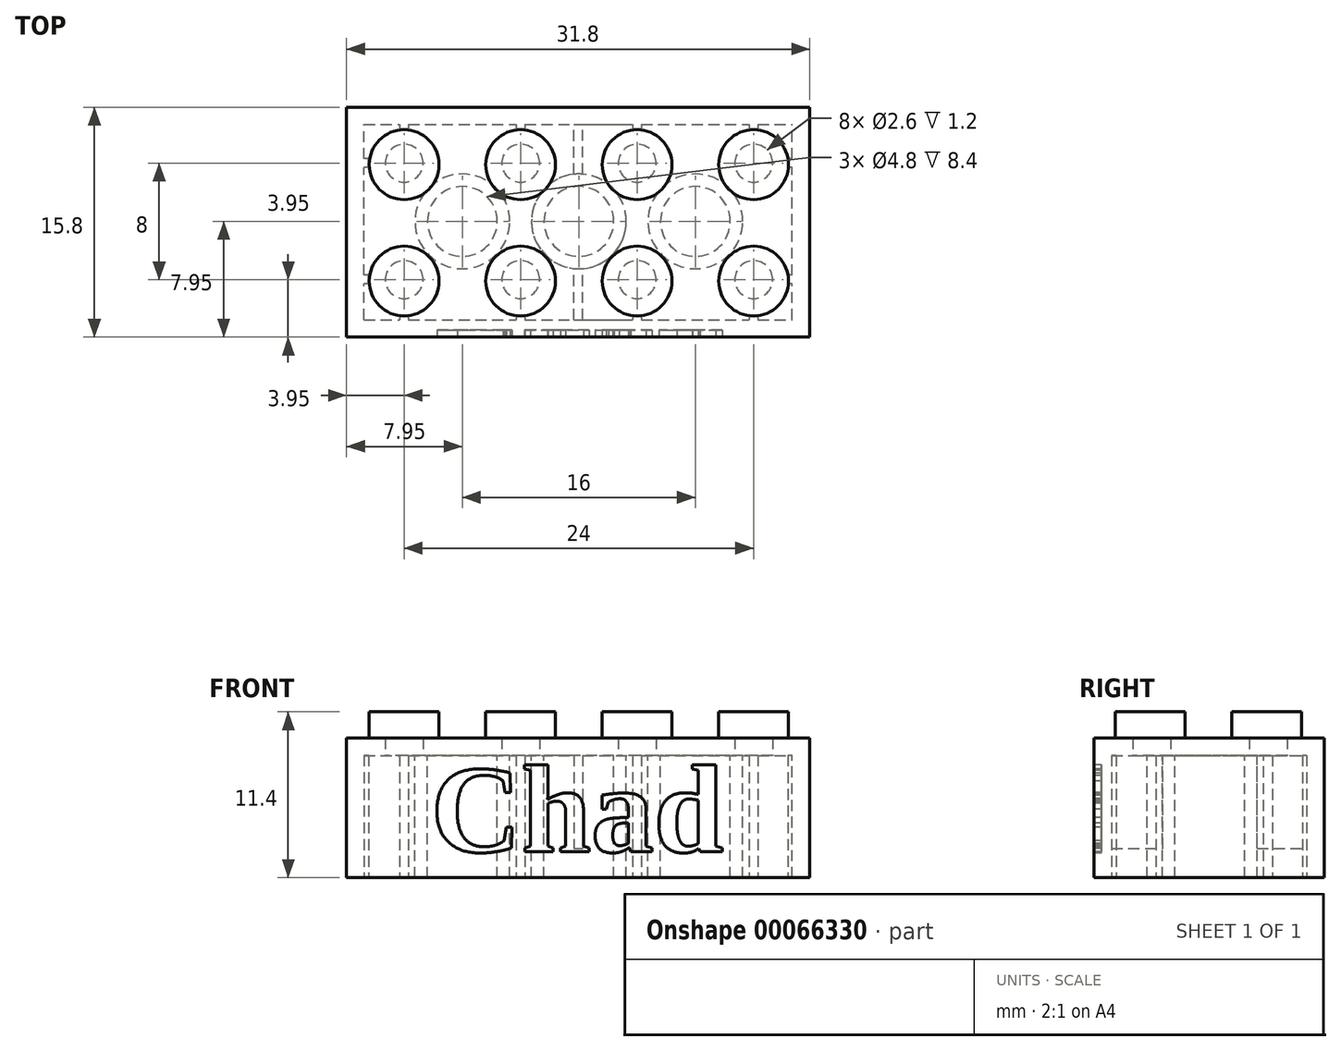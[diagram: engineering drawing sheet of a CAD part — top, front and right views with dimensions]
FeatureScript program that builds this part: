
annotation { "Feature Type Name" : "Feature", "Feature Type Description" : "" }
export const myFeature = defineFeature(function(context is Context, id is Id, definition is map)
    precondition{}
    {
        {
            var Q0;
            Q0=qCreatedBy(makeId("Top.planeOp"),FACE);
            var sketch = newSketch(context, id + "F0", { "sketchPlane" : qUnion([Q0])});
            skLineSegment(sketch, "E0.rect.bottom", {"start": v(15.9, 7.9) * mm, "end": v(-15.9, 7.9) * mm});
            skLineSegment(sketch, "E0.rect.top", {"start": v(15.9, -7.9) * mm, "end": v(-15.9, -7.9) * mm});
            skLineSegment(sketch, "E0.rect.left", {"start": v(15.9, 7.9) * mm, "end": v(15.9, -7.9) * mm});
            skLineSegment(sketch, "E0.rect.right", {"start": v(-15.9, 7.9) * mm, "end": v(-15.9, -7.9) * mm});
            skPoint(sketch, "E0.rect.middle", {"position": v(0, 0) * mm});
            skSolve(sketch);
        }
        {
            var Q0;
            Q0 = qSketchRegion(id + "F0", true);
            extrude(context, id + "F1", {"entities" : qUnion([Q0]), "depth" : 9.6 * mm});
        }
        {
            var Q0;
            Q0=makeQuery(id+"F0.imprint","IMPRINT",FACE,{"disambiguationData":[TD([[makeQuery(id+"F0.imprint","IMPRINT",EDGE,{"derivedFrom":sQuery(id+"F0.wireOp",EDGE,"E0.rect.bottom")}),1.0]])]});
            var sketch = newSketch(context, id + "F2", { "sketchPlane" : qUnion([Q0])});
            skLineSegment(sketch, "E1.rect.bottom", {"start": v(-14.7, -6.7) * mm, "end": v(14.7, -6.7) * mm});
            skLineSegment(sketch, "E1.rect.top", {"start": v(-14.7, 6.7) * mm, "end": v(14.7, 6.7) * mm});
            skLineSegment(sketch, "E1.rect.left", {"start": v(-14.7, -6.7) * mm, "end": v(-14.7, 6.7) * mm});
            skLineSegment(sketch, "E1.rect.right", {"start": v(14.7, -6.7) * mm, "end": v(14.7, 6.7) * mm});
            skPoint(sketch, "E1.rect.middle", {"position": v(0, 0) * mm});
            skSolve(sketch);
        }
        {
            var Q0;
            Q0 = qSketchRegion(id + "F2", true);
            extrude(context, id + "F3", {"entities" : qUnion([Q0]), "operationType" : NewBodyOperationType.REMOVE, "depth" : 8.4 * mm});
        }
        {
            var Q0;
            Q0=makeQuery(id+"F1.opExtrude","CAP_FACE",FACE,{"disambiguationData":[OSD([sQuery(id+"F0.wireOp",EDGE,"E0.rect.bottom"),sQuery(id+"F0.wireOp",EDGE,"E0.rect.top"),sQuery(id+"F0.wireOp",EDGE,"E0.rect.left"),sQuery(id+"F0.wireOp",EDGE,"E0.rect.right")])],"isStart":false});
            var sketch = newSketch(context, id + "F4", { "sketchPlane" : qUnion([Q0])});
            skLineSegment(sketch, "E2", {"start": v(-22.58, 0) * mm, "end": v(20.72, 0) * mm, "construction": true});
            skPoint(sketch, "E2.endSnap0", {"position": v(15.9, 0) * mm});
            skCircle(sketch, "E3", {"center": v(-11.95, 3.95) * mm, "radius": 2.4 * mm});
            skCircle(sketch, "E4.0.1.0", {"center": v(-11.95, -4.05) * mm, "radius": 2.4 * mm});
            skCircle(sketch, "E4.1.0.0", {"center": v(-3.95, 3.95) * mm, "radius": 2.4 * mm});
            skCircle(sketch, "E4.1.1.0", {"center": v(-3.95, -4.05) * mm, "radius": 2.4 * mm});
            skCircle(sketch, "E4.2.0.0", {"center": v(4.05, 3.95) * mm, "radius": 2.4 * mm});
            skCircle(sketch, "E4.2.1.0", {"center": v(4.05, -4.05) * mm, "radius": 2.4 * mm});
            skCircle(sketch, "E4.3.0.0", {"center": v(12.05, 3.95) * mm, "radius": 2.4 * mm});
            skCircle(sketch, "E4.3.1.0", {"center": v(12.05, -4.05) * mm, "radius": 2.4 * mm});
            skLineSegment(sketch, "E4.direction1", {"start": v(-11.95, 3.95) * mm, "end": v(-3.95, 3.95) * mm, "construction": true});
            skLineSegment(sketch, "E4.direction2", {"start": v(-11.95, 3.95) * mm, "end": v(-11.95, -4.05) * mm, "construction": true});
            skSolve(sketch);
        }
        {
            var Q0;
            Q0 = qSketchRegion(id + "F4", true);
            extrude(context, id + "F5", {"entities" : qUnion([Q0]), "operationType" : NewBodyOperationType.ADD, "depth" : 1.8 * mm});
        }
        {
            var Q0;
            Q0=qCreatedBy(makeId("Top.planeOp"),FACE);
            cPlane(context, id + "F6", {"entities" : qUnion([Q0]), "cplaneType" : CPlaneType.OFFSET, "offset" : 8.4 * mm, "width" : 150 * mm, "height" : 150 * mm});
        }
        {
            var Q0;
            Q0=qCreatedBy(id+"F6.planeOp",FACE);
            var sketch = newSketch(context, id + "F7", { "sketchPlane" : qUnion([Q0])});
            skCircle(sketch, "E5", {"center": v(-11.95, -3.95) * mm, "radius": 1.3 * mm});
            skCircle(sketch, "E6.0.1.0", {"center": v(-11.95, 4.05) * mm, "radius": 1.3 * mm});
            skCircle(sketch, "E6.1.0.0", {"center": v(-3.95, -3.95) * mm, "radius": 1.3 * mm});
            skCircle(sketch, "E6.1.1.0", {"center": v(-3.95, 4.05) * mm, "radius": 1.3 * mm});
            skCircle(sketch, "E6.2.0.0", {"center": v(4.05, -3.95) * mm, "radius": 1.3 * mm});
            skCircle(sketch, "E6.2.1.0", {"center": v(4.05, 4.05) * mm, "radius": 1.3 * mm});
            skCircle(sketch, "E6.3.0.0", {"center": v(12.05, -3.95) * mm, "radius": 1.3 * mm});
            skCircle(sketch, "E6.3.1.0", {"center": v(12.05, 4.05) * mm, "radius": 1.3 * mm});
            skLineSegment(sketch, "E6.direction1", {"start": v(-11.95, -3.95) * mm, "end": v(-3.95, -3.95) * mm, "construction": true});
            skLineSegment(sketch, "E6.direction2", {"start": v(-11.95, -3.95) * mm, "end": v(-11.95, 4.05) * mm, "construction": true});
            skSolve(sketch);
        }
        {
            var Q0;
            Q0 = qSketchRegion(id + "F7", true);
            extrude(context, id + "F8", {"entities" : qUnion([Q0]), "operationType" : NewBodyOperationType.REMOVE, "depth" : 1.2 * mm});
        }
        {
            var Q0;
            Q0=qCreatedBy(id+"F6.planeOp",FACE);
            var sketch = newSketch(context, id + "F9", { "sketchPlane" : qUnion([Q0])});
            skLineSegment(sketch, "E7", {"start": v(-11.95, -3.95) * mm, "end": v(-3.95, 4.05) * mm, "construction": true});
            skLineSegment(sketch, "E8", {"start": v(-11.95, 4.05) * mm, "end": v(-3.95, -3.95) * mm, "construction": true});
            skLineSegment(sketch, "E9", {"start": v(-3.95, -3.95) * mm, "end": v(4.05, 4.05) * mm, "construction": true});
            skLineSegment(sketch, "E10", {"start": v(4.05, 4.05) * mm, "end": v(12.05, -3.95) * mm, "construction": true});
            skLineSegment(sketch, "E11", {"start": v(-3.95, 4.05) * mm, "end": v(4.05, -3.95) * mm, "construction": true});
            skLineSegment(sketch, "E12", {"start": v(4.05, -3.95) * mm, "end": v(12.05, 4.05) * mm, "construction": true});
            skPoint(sketch, "E13", {"position": v(-7.95, 0.05) * mm});
            skPoint(sketch, "E14", {"position": v(0, 0) * mm});
            skPoint(sketch, "E15", {"position": v(8.05, 0) * mm});
            skPoint(sketch, "E15.positionSnap0", {"position": v(8.05, 0.05) * mm});
            skCircle(sketch, "E16", {"center": v(-7.95, 0.05) * mm, "radius": 2.4 * mm});
            skCircle(sketch, "E17", {"center": v(-7.95, 0.05) * mm, "radius": 3.25 * mm});
            skCircle(sketch, "E18.1.0.0", {"center": v(0.05, 0.05) * mm, "radius": 3.25 * mm});
            skCircle(sketch, "E18.2.0.0", {"center": v(8.05, 0.05) * mm, "radius": 3.25 * mm});
            skLineSegment(sketch, "E18.direction1", {"start": v(-7.95, 0.05) * mm, "end": v(0.05, 0.05) * mm, "construction": true});
            skCircle(sketch, "E19.1.0.0", {"center": v(0.05, 0.05) * mm, "radius": 2.4 * mm});
            skCircle(sketch, "E19.2.0.0", {"center": v(8.05, 0.05) * mm, "radius": 2.4 * mm});
            skSolve(sketch);
        }
        {
            var Q0;
            Q0 = qSketchRegion(id + "F9", true);
            var Q1;
            Q1=makeQuery(id+"F1.opExtrude","CAP_FACE",FACE,{"disambiguationData":[OSD([sQuery(id+"F0.wireOp",EDGE,"E0.rect.bottom"),sQuery(id+"F0.wireOp",EDGE,"E0.rect.top"),sQuery(id+"F0.wireOp",EDGE,"E0.rect.left"),sQuery(id+"F0.wireOp",EDGE,"E0.rect.right")])],"isStart":true});
            extrude(context, id + "F10", {"entities" : qUnion([Q0]), "operationType" : NewBodyOperationType.ADD, "endBound" : BoundingType.UP_TO_SURFACE, "oppositeDirection" : true, "endBoundEntityFace" : qUnion([Q1]), "depth" : 7.15 * mm});
        }
        {
            var Q0;
            Q0=makeQuery(id+"F1.opExtrude","SWEPT_FACE",FACE,{"disambiguationData":[OSD([sQuery(id+"F0.wireOp",EDGE,"E0.rect.top")])]});
            var sketch = newSketch(context, id + "F11", { "sketchPlane" : qUnion([Q0])});
            skText(sketch, "E20", { "text": "Chad", "fontName": "Tinos-Bold.ttf"});
            const initialGuessF11  = {"E20": [-0.01012, 0.00178, 1, 0, 0.0062]};
            skSetInitialGuess(sketch, initialGuessF11);
            skSolve(sketch);
        }
        {
            var Q0;
            Q0 = qSketchRegion(id + "F11", true);
            extrude(context, id + "F12", {"entities" : qUnion([Q0]), "operationType" : NewBodyOperationType.REMOVE, "oppositeDirection" : true, "depth" : 0.5 * mm});
        }
        {
            var Q0;
            Q0=makeQuery(id+"F0.imprint","IMPRINT",FACE,{"disambiguationData":[TD([[makeQuery(id+"F0.imprint","IMPRINT",EDGE,{"derivedFrom":sQuery(id+"F0.wireOp",EDGE,"E0.rect.bottom")}),1.0]])]});
            var sketch = newSketch(context, id + "F13", { "sketchPlane" : qUnion([Q0])});
            skLineSegment(sketch, "E21", {"start": v(-11.95, -4.07) * mm, "end": v(-11.95, 4.05) * mm, "construction": true});
            skLineSegment(sketch, "E22.rect.bottom", {"start": v(-11.65, -6.4) * mm, "end": v(-12.25, -6.4) * mm});
            skLineSegment(sketch, "E22.rect.top", {"start": v(-11.65, -6.7) * mm, "end": v(-12.25, -6.7) * mm});
            skLineSegment(sketch, "E22.rect.left", {"start": v(-11.65, -6.4) * mm, "end": v(-11.65, -6.7) * mm});
            skLineSegment(sketch, "E22.rect.right", {"start": v(-12.25, -6.4) * mm, "end": v(-12.25, -6.7) * mm});
            skPoint(sketch, "E22.rect.middle", {"position": v(-11.95, -6.55) * mm});
            skLineSegment(sketch, "E23", {"start": v(-11.95, -7.49) * mm, "end": v(-11.95, 4.05) * mm, "construction": true});
            skLineSegment(sketch, "E24.0.1.0", {"start": v(-11.65, 6.7) * mm, "end": v(-11.65, 6.4) * mm});
            skLineSegment(sketch, "E24.0.1.1", {"start": v(-11.65, 6.4) * mm, "end": v(-12.25, 6.4) * mm});
            skLineSegment(sketch, "E24.0.1.2", {"start": v(-12.25, 6.7) * mm, "end": v(-12.25, 6.4) * mm});
            skLineSegment(sketch, "E24.0.1.3", {"start": v(-11.65, 6.7) * mm, "end": v(-12.25, 6.7) * mm});
            skLineSegment(sketch, "E24.1.0.0", {"start": v(-3.65, -6.4) * mm, "end": v(-3.65, -6.7) * mm});
            skLineSegment(sketch, "E24.1.0.1", {"start": v(-3.65, -6.7) * mm, "end": v(-4.25, -6.7) * mm});
            skLineSegment(sketch, "E24.1.0.2", {"start": v(-4.25, -6.4) * mm, "end": v(-4.25, -6.7) * mm});
            skLineSegment(sketch, "E24.1.0.3", {"start": v(-3.65, -6.4) * mm, "end": v(-4.25, -6.4) * mm});
            skLineSegment(sketch, "E24.1.1.0", {"start": v(-3.65, 6.7) * mm, "end": v(-3.65, 6.4) * mm});
            skLineSegment(sketch, "E24.1.1.1", {"start": v(-3.65, 6.4) * mm, "end": v(-4.25, 6.4) * mm});
            skLineSegment(sketch, "E24.1.1.2", {"start": v(-4.25, 6.7) * mm, "end": v(-4.25, 6.4) * mm});
            skLineSegment(sketch, "E24.1.1.3", {"start": v(-3.65, 6.7) * mm, "end": v(-4.25, 6.7) * mm});
            skLineSegment(sketch, "E24.2.0.0", {"start": v(4.35, -6.4) * mm, "end": v(4.35, -6.7) * mm});
            skLineSegment(sketch, "E24.2.0.1", {"start": v(4.35, -6.7) * mm, "end": v(3.75, -6.7) * mm});
            skLineSegment(sketch, "E24.2.0.2", {"start": v(3.75, -6.4) * mm, "end": v(3.75, -6.7) * mm});
            skLineSegment(sketch, "E24.2.0.3", {"start": v(4.35, -6.4) * mm, "end": v(3.75, -6.4) * mm});
            skLineSegment(sketch, "E24.2.1.0", {"start": v(4.35, 6.7) * mm, "end": v(4.35, 6.4) * mm});
            skLineSegment(sketch, "E24.2.1.1", {"start": v(4.35, 6.4) * mm, "end": v(3.75, 6.4) * mm});
            skLineSegment(sketch, "E24.2.1.2", {"start": v(3.75, 6.7) * mm, "end": v(3.75, 6.4) * mm});
            skLineSegment(sketch, "E24.2.1.3", {"start": v(4.35, 6.7) * mm, "end": v(3.75, 6.7) * mm});
            skLineSegment(sketch, "E24.3.0.0", {"start": v(12.35, -6.4) * mm, "end": v(12.35, -6.7) * mm});
            skLineSegment(sketch, "E24.3.0.1", {"start": v(12.35, -6.7) * mm, "end": v(11.75, -6.7) * mm});
            skLineSegment(sketch, "E24.3.0.2", {"start": v(11.75, -6.4) * mm, "end": v(11.75, -6.7) * mm});
            skLineSegment(sketch, "E24.3.0.3", {"start": v(12.35, -6.4) * mm, "end": v(11.75, -6.4) * mm});
            skLineSegment(sketch, "E24.3.1.0", {"start": v(12.35, 6.7) * mm, "end": v(12.35, 6.4) * mm});
            skLineSegment(sketch, "E24.3.1.1", {"start": v(12.35, 6.4) * mm, "end": v(11.75, 6.4) * mm});
            skLineSegment(sketch, "E24.3.1.2", {"start": v(11.75, 6.7) * mm, "end": v(11.75, 6.4) * mm});
            skLineSegment(sketch, "E24.3.1.3", {"start": v(12.35, 6.7) * mm, "end": v(11.75, 6.7) * mm});
            skLineSegment(sketch, "E24.direction1", {"start": v(-11.65, -6.7) * mm, "end": v(-3.65, -6.7) * mm, "construction": true});
            skLineSegment(sketch, "E24.direction2", {"start": v(-11.65, -6.7) * mm, "end": v(-11.65, 6.4) * mm, "construction": true});
            skSolve(sketch);
        }
        {
            var Q0;
            Q0 = qSketchRegion(id + "F13", true);
            var Q1;
            {var subQ0=sQuery(id+"F2.wireOp",EDGE,"E1.rect.bottom");var subQ1=sQuery(id+"F2.wireOp",EDGE,"E1.rect.top");var subQ2=sQuery(id+"F2.wireOp",EDGE,"E1.rect.left");var subQ3=sQuery(id+"F2.wireOp",EDGE,"E1.rect.right");Q1=makeQuery(id+"F10.boolean.opBoolean","SPLIT",FACE,{"disambiguationData":[TD([makeQuery(id+"F3.boolean.opBoolean","COPY",FACE,{"derivedFrom":makeQuery(id+"F3.opExtrude","SWEPT_FACE",FACE,{"disambiguationData":[OSD([subQ0])]})})])],"derivedFrom":makeQuery(id+"F3.boolean.opBoolean","COPY",FACE,{"derivedFrom":makeQuery(id+"F3.opExtrude","CAP_FACE",FACE,{"disambiguationData":[OSD([subQ0,subQ1,subQ2,subQ3])],"isStart":false})})});}
            extrude(context, id + "F14", {"entities" : qUnion([Q0]), "operationType" : NewBodyOperationType.ADD, "endBound" : BoundingType.UP_TO_SURFACE, "endBoundEntityFace" : qUnion([Q1]), "depth" : 25 * mm});
        }
        {
            var Q0;
            Q0=makeQuery(id+"F0.imprint","IMPRINT",FACE,{"disambiguationData":[TD([[makeQuery(id+"F0.imprint","IMPRINT",EDGE,{"derivedFrom":sQuery(id+"F0.wireOp",EDGE,"E0.rect.bottom")}),1.0]])]});
            var sketch = newSketch(context, id + "F15", { "sketchPlane" : qUnion([Q0])});
            skLineSegment(sketch, "E25", {"start": v(-11.95, -3.95) * mm, "end": v(-15.23, -3.95) * mm, "construction": true});
            skLineSegment(sketch, "E26.rect.bottom", {"start": v(-14.4, -4.25) * mm, "end": v(-14.7, -4.25) * mm});
            skLineSegment(sketch, "E26.rect.top", {"start": v(-14.4, -3.65) * mm, "end": v(-14.7, -3.65) * mm});
            skLineSegment(sketch, "E26.rect.left", {"start": v(-14.4, -4.25) * mm, "end": v(-14.4, -3.65) * mm});
            skLineSegment(sketch, "E26.rect.right", {"start": v(-14.7, -4.25) * mm, "end": v(-14.7, -3.65) * mm});
            skPoint(sketch, "E26.rect.middle", {"position": v(-14.55, -3.95) * mm});
            skLineSegment(sketch, "E27.0.1.0", {"start": v(-14.4, 3.75) * mm, "end": v(-14.4, 4.35) * mm});
            skLineSegment(sketch, "E27.0.1.1", {"start": v(-14.4, 3.75) * mm, "end": v(-14.7, 3.75) * mm});
            skLineSegment(sketch, "E27.0.1.2", {"start": v(-14.7, 3.75) * mm, "end": v(-14.7, 4.35) * mm});
            skLineSegment(sketch, "E27.0.1.3", {"start": v(-14.4, 4.35) * mm, "end": v(-14.7, 4.35) * mm});
            skLineSegment(sketch, "E27.1.0.0", {"start": v(14.7, -4.25) * mm, "end": v(14.7, -3.65) * mm});
            skLineSegment(sketch, "E27.1.0.1", {"start": v(14.7, -4.25) * mm, "end": v(14.4, -4.25) * mm});
            skLineSegment(sketch, "E27.1.0.2", {"start": v(14.4, -4.25) * mm, "end": v(14.4, -3.65) * mm});
            skLineSegment(sketch, "E27.1.0.3", {"start": v(14.7, -3.65) * mm, "end": v(14.4, -3.65) * mm});
            skLineSegment(sketch, "E27.1.1.0", {"start": v(14.7, 3.75) * mm, "end": v(14.7, 4.35) * mm});
            skLineSegment(sketch, "E27.1.1.1", {"start": v(14.7, 3.75) * mm, "end": v(14.4, 3.75) * mm});
            skLineSegment(sketch, "E27.1.1.2", {"start": v(14.4, 3.75) * mm, "end": v(14.4, 4.35) * mm});
            skLineSegment(sketch, "E27.1.1.3", {"start": v(14.7, 4.35) * mm, "end": v(14.4, 4.35) * mm});
            skLineSegment(sketch, "E27.direction1", {"start": v(-14.4, -4.25) * mm, "end": v(14.7, -4.25) * mm, "construction": true});
            skLineSegment(sketch, "E27.direction2", {"start": v(-14.4, -4.25) * mm, "end": v(-14.4, 3.75) * mm, "construction": true});
            skSolve(sketch);
        }
        {
            var Q0;
            Q0 = qSketchRegion(id + "F15", true);
            var Q1;
            {var subQ0=sQuery(id+"F2.wireOp",EDGE,"E1.rect.bottom");var subQ1=sQuery(id+"F2.wireOp",EDGE,"E1.rect.top");var subQ2=sQuery(id+"F2.wireOp",EDGE,"E1.rect.left");var subQ3=sQuery(id+"F2.wireOp",EDGE,"E1.rect.right");Q1=makeQuery(id+"F10.boolean.opBoolean","SPLIT",FACE,{"disambiguationData":[TD([makeQuery(id+"F3.boolean.opBoolean","COPY",FACE,{"derivedFrom":makeQuery(id+"F3.opExtrude","SWEPT_FACE",FACE,{"disambiguationData":[OSD([subQ0])]})})])],"derivedFrom":makeQuery(id+"F3.boolean.opBoolean","COPY",FACE,{"derivedFrom":makeQuery(id+"F3.opExtrude","CAP_FACE",FACE,{"disambiguationData":[OSD([subQ0,subQ1,subQ2,subQ3])],"isStart":false})})});}
            extrude(context, id + "F16", {"entities" : qUnion([Q0]), "operationType" : NewBodyOperationType.ADD, "endBound" : BoundingType.UP_TO_SURFACE, "endBoundEntityFace" : qUnion([Q1]), "depth" : 25 * mm});
        }
        {
            var Q0;
            Q0=qCreatedBy(id+"F6.planeOp",FACE);
            var sketch = newSketch(context, id + "F17", { "sketchPlane" : qUnion([Q0])});
            skLineSegment(sketch, "E28.rect.bottom", {"start": v(0.3, 2.9) * mm, "end": v(-0.3, 2.9) * mm});
            skLineSegment(sketch, "E28.rect.top", {"start": v(0.3, 6.9) * mm, "end": v(-0.3, 6.9) * mm});
            skLineSegment(sketch, "E28.rect.left", {"start": v(0.3, 2.9) * mm, "end": v(0.3, 6.9) * mm});
            skLineSegment(sketch, "E28.rect.right", {"start": v(-0.3, 2.9) * mm, "end": v(-0.3, 6.9) * mm});
            skPoint(sketch, "E28.rect.middle", {"position": v(0, 4.9) * mm});
            skLineSegment(sketch, "E29.0.1.0", {"start": v(-0.3, -6.93) * mm, "end": v(-0.3, -2.93) * mm});
            skLineSegment(sketch, "E29.0.1.1", {"start": v(0.3, -6.93) * mm, "end": v(0.3, -2.93) * mm});
            skLineSegment(sketch, "E29.0.1.2", {"start": v(0.3, -2.93) * mm, "end": v(-0.3, -2.93) * mm});
            skLineSegment(sketch, "E29.0.1.3", {"start": v(0.3, -6.93) * mm, "end": v(-0.3, -6.93) * mm});
            skLineSegment(sketch, "E29.direction1", {"start": v(-0.3, 2.9) * mm, "end": v(24.7, 2.9) * mm, "construction": true});
            skLineSegment(sketch, "E29.direction2", {"start": v(-0.3, 2.9) * mm, "end": v(-0.3, -6.93) * mm, "construction": true});
            skSolve(sketch);
        }
        {
            var Q0;
            Q0 = qSketchRegion(id + "F17", true);
            extrude(context, id + "F18", {"entities" : qUnion([Q0]), "operationType" : NewBodyOperationType.ADD, "oppositeDirection" : true, "depth" : 6.4 * mm});
        }
    });
